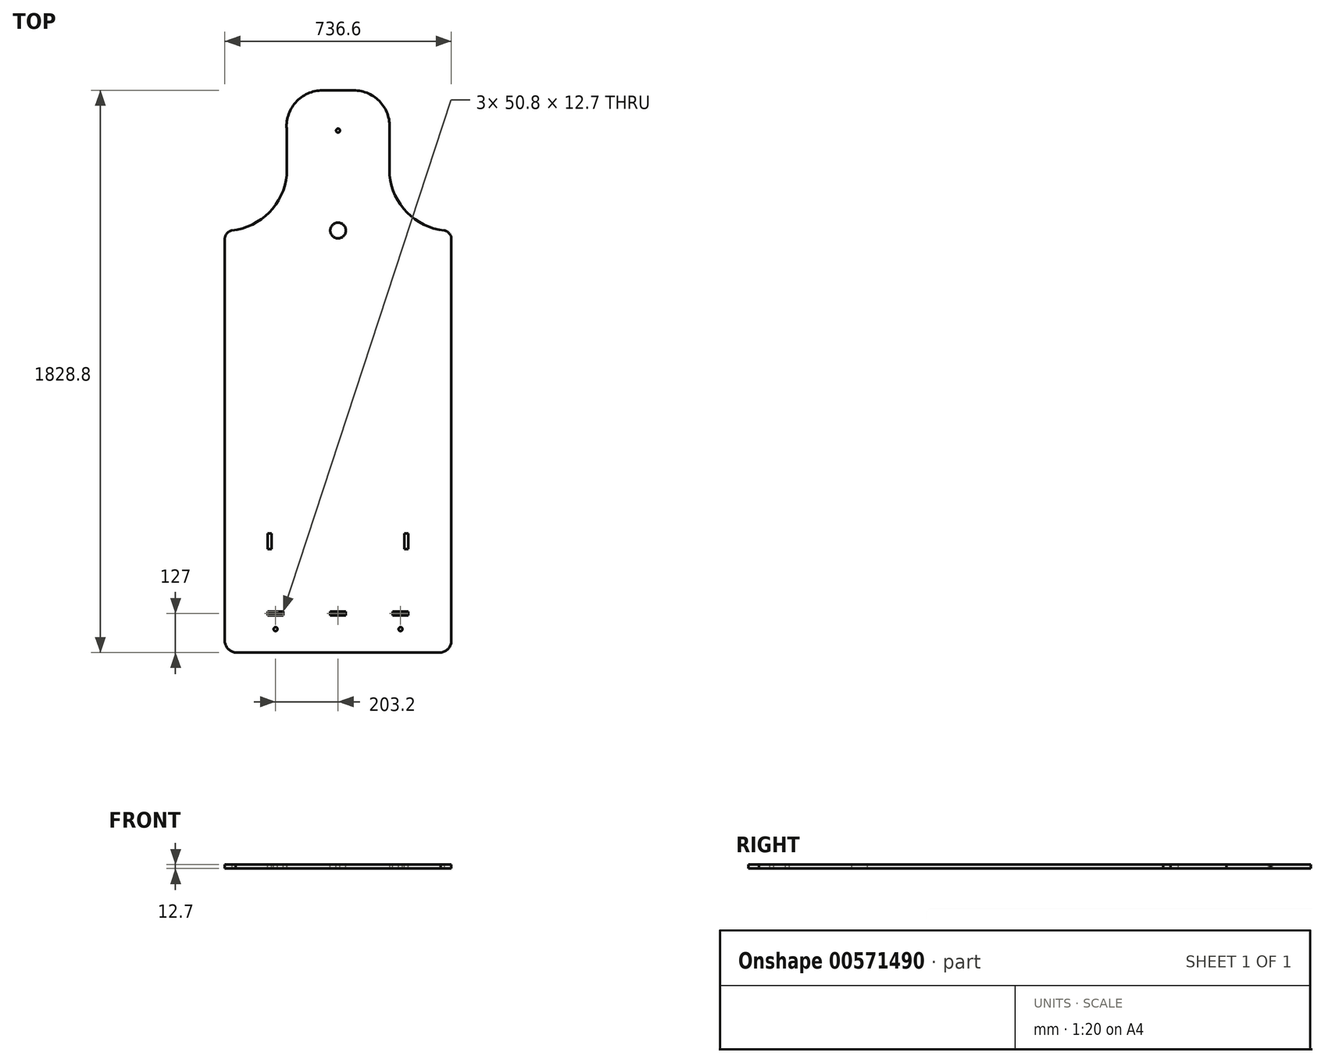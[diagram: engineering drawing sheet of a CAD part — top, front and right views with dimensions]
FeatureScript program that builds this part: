
annotation { "Feature Type Name" : "Feature", "Feature Type Description" : "" }
export const myFeature = defineFeature(function(context is Context, id is Id, definition is map)
    precondition{}
    {
        {
            var Q0;
            Q0=qCreatedBy(makeId("Top.planeOp"),FACE);
            var sketch = newSketch(context, id + "F0", { "sketchPlane" : qUnion([Q0])});
            skLineSegment(sketch, "E0.bottom", {"start": v(333.07, -685.8) * mm, "end": v(-333.07, -685.8) * mm});
            skLineSegment(sketch, "E0.left", {"start": v(368.3, -652.17) * mm, "end": v(368.3, 662.5) * mm});
            skLineSegment(sketch, "E0.right", {"start": v(-368.3, -652.17) * mm, "end": v(-368.3, 662.5) * mm});
            skPoint(sketch, "E0.middle", {"position": v(0, 0) * mm});
            skLineSegment(sketch, "E1", {"start": v(0, 685.8) * mm, "end": v(0, 1143) * mm, "construction": true});
            skPoint(sketch, "E1.endSnap0", {"position": v(0, 685.8) * mm});
            skLineSegment(sketch, "E2", {"start": v(0, 1143) * mm, "end": v(-50.8, 1143) * mm});
            skLineSegment(sketch, "E3", {"start": v(0, 1143) * mm, "end": v(50.8, 1143) * mm});
            skArc(sketch, "E4", {"start": v(-50.8, 1143) * mm, "mid": v(-138.23, 1103.66) * mm, "end": v(-166.78, 1012.14) * mm});
            skArc(sketch, "E5.MirrorCS", {"start": v(50.8, 1143) * mm, "mid": v(138.23, 1103.66) * mm, "end": v(166.78, 1012.14) * mm});
            skLineSegment(sketch, "E6", {"start": v(-166.78, 1012.14) * mm, "end": v(-166.78, 867.84) * mm});
            skArc(sketch, "E7", {"start": v(-345.55, 687.08) * mm, "mid": v(-224.28, 745.92) * mm, "end": v(-166.78, 867.84) * mm});
            skArc(sketch, "E8.MirrorCS", {"start": v(345.55, 687.08) * mm, "mid": v(224.28, 745.92) * mm, "end": v(166.78, 867.84) * mm});
            skLineSegment(sketch, "E9.MirrorCS", {"start": v(166.78, 1012.14) * mm, "end": v(166.78, 867.84) * mm});
            skArc(sketch, "E10", {"start": v(-345.55, 687.08) * mm, "mid": v(-360.85, 678.42) * mm, "end": v(-368.3, 662.5) * mm});
            skArc(sketch, "E11.MirrorCS", {"start": v(345.55, 687.08) * mm, "mid": v(360.85, 678.42) * mm, "end": v(368.3, 662.5) * mm});
            skPoint(sketch, "E12.orphan", {"position": v(-368.3, 685.8) * mm});
            skPoint(sketch, "E13.orphan", {"position": v(368.3, 685.8) * mm});
            skPoint(sketch, "E14.orphan", {"position": v(368.3, 655.07) * mm});
            skPoint(sketch, "E15.orphan", {"position": v(-368.3, 655.07) * mm});
            skArc(sketch, "E16", {"start": v(-368.3, -652.17) * mm, "mid": v(-356.47, -675.05) * mm, "end": v(-333.07, -685.8) * mm});
            skLineSegment(sketch, "E17", {"start": v(0, -685.8) * mm, "end": v(0, -615.78) * mm, "construction": true});
            skArc(sketch, "E18.MirrorCS", {"start": v(368.3, -652.17) * mm, "mid": v(356.47, -675.05) * mm, "end": v(333.07, -685.8) * mm});
            skPoint(sketch, "E19.orphan", {"position": v(-368.3, -685.8) * mm});
            skPoint(sketch, "E20.orphan", {"position": v(368.3, -685.8) * mm});
            skPoint(sketch, "E21.orphan", {"position": v(368.3, -640.65) * mm});
            skPoint(sketch, "E22.orphan", {"position": v(-368.3, -640.65) * mm});
            skSolve(sketch);
        }
        {
            var Q0;
            Q0 = qSketchRegion(id + "F0", true);
            extrude(context, id + "F1", {"entities" : qUnion([Q0]), "depth" : 12.7 * mm, "offsetDistance" : 25.4 * mm});
        }
        {
            var Q0;
            Q0=makeQuery(id+"F1.opExtrude","CAP_FACE",FACE,{"disambiguationData":[OSD([sQuery(id+"F0.wireOp",EDGE,"E0.bottom"),sQuery(id+"F0.wireOp",EDGE,"E0.left"),sQuery(id+"F0.wireOp",EDGE,"E0.right"),sQuery(id+"F0.wireOp",EDGE,"E2"),sQuery(id+"F0.wireOp",EDGE,"E3"),sQuery(id+"F0.wireOp",EDGE,"E4"),sQuery(id+"F0.wireOp",EDGE,"E5.MirrorCS"),sQuery(id+"F0.wireOp",EDGE,"E6"),sQuery(id+"F0.wireOp",EDGE,"E7"),sQuery(id+"F0.wireOp",EDGE,"E8.MirrorCS"),sQuery(id+"F0.wireOp",EDGE,"E9.MirrorCS"),sQuery(id+"F0.wireOp",EDGE,"E10"),sQuery(id+"F0.wireOp",EDGE,"E11.MirrorCS"),sQuery(id+"F0.wireOp",EDGE,"E16"),sQuery(id+"F0.wireOp",EDGE,"E18.MirrorCS")])],"isStart":false});
            var sketch = newSketch(context, id + "F2", { "sketchPlane" : qUnion([Q0])});
            skCircle(sketch, "E23", {"center": v(0, 1012.14) * mm, "radius": 6.35 * mm});
            skSolve(sketch);
        }
        {
            var Q0;
            Q0 = qSketchRegion(id + "F2", true);
            extrude(context, id + "F3", {"entities" : qUnion([Q0]), "operationType" : NewBodyOperationType.REMOVE, "oppositeDirection" : true, "depth" : 25.4 * mm, "offsetDistance" : 25.4 * mm});
        }
        {
            var Q0;
            Q0=makeQuery(id+"F1.opExtrude","CAP_FACE",FACE,{"disambiguationData":[OSD([sQuery(id+"F0.wireOp",EDGE,"E0.bottom"),sQuery(id+"F0.wireOp",EDGE,"E0.left"),sQuery(id+"F0.wireOp",EDGE,"E0.right"),sQuery(id+"F0.wireOp",EDGE,"E2"),sQuery(id+"F0.wireOp",EDGE,"E3"),sQuery(id+"F0.wireOp",EDGE,"E4"),sQuery(id+"F0.wireOp",EDGE,"E5.MirrorCS"),sQuery(id+"F0.wireOp",EDGE,"E6"),sQuery(id+"F0.wireOp",EDGE,"E7"),sQuery(id+"F0.wireOp",EDGE,"E8.MirrorCS"),sQuery(id+"F0.wireOp",EDGE,"E9.MirrorCS"),sQuery(id+"F0.wireOp",EDGE,"E10"),sQuery(id+"F0.wireOp",EDGE,"E11.MirrorCS"),sQuery(id+"F0.wireOp",EDGE,"E16"),sQuery(id+"F0.wireOp",EDGE,"E18.MirrorCS")])],"isStart":false});
            var sketch = newSketch(context, id + "F4", { "sketchPlane" : qUnion([Q0])});
            skPoint(sketch, "E24.endSnap0", {"position": v(0, -685.8) * mm});
            skPoint(sketch, "E25.endSnap0", {"position": v(0, -609.6) * mm});
            skCircle(sketch, "E26", {"center": v(-203.2, -609.6) * mm, "radius": 6.35 * mm});
            skCircle(sketch, "E27.MirrorC", {"center": v(203.2, -609.6) * mm, "radius": 6.35 * mm});
            skSolve(sketch);
        }
        {
            var Q0;
            Q0 = qSketchRegion(id + "F4", true);
            extrude(context, id + "F5", {"entities" : qUnion([Q0]), "operationType" : NewBodyOperationType.REMOVE, "oppositeDirection" : true, "depth" : 25.4 * mm, "offsetDistance" : 25.4 * mm});
        }
        {
            var Q0;
            Q0=makeQuery(id+"F1.opExtrude","CAP_FACE",FACE,{"disambiguationData":[OSD([sQuery(id+"F0.wireOp",EDGE,"E0.bottom"),sQuery(id+"F0.wireOp",EDGE,"E0.left"),sQuery(id+"F0.wireOp",EDGE,"E0.right"),sQuery(id+"F0.wireOp",EDGE,"E2"),sQuery(id+"F0.wireOp",EDGE,"E3"),sQuery(id+"F0.wireOp",EDGE,"E4"),sQuery(id+"F0.wireOp",EDGE,"E5.MirrorCS"),sQuery(id+"F0.wireOp",EDGE,"E6"),sQuery(id+"F0.wireOp",EDGE,"E7"),sQuery(id+"F0.wireOp",EDGE,"E8.MirrorCS"),sQuery(id+"F0.wireOp",EDGE,"E9.MirrorCS"),sQuery(id+"F0.wireOp",EDGE,"E10"),sQuery(id+"F0.wireOp",EDGE,"E11.MirrorCS"),sQuery(id+"F0.wireOp",EDGE,"E16"),sQuery(id+"F0.wireOp",EDGE,"E18.MirrorCS")])],"isStart":false});
            var sketch = newSketch(context, id + "F6", { "sketchPlane" : qUnion([Q0])});
            skLineSegment(sketch, "E28", {"start": v(-345.55, 687.08) * mm, "end": v(345.55, 687.08) * mm, "construction": true});
            skLineSegment(sketch, "E29", {"start": v(0, 687.08) * mm, "end": v(0, 77.48) * mm, "construction": true});
            skCircle(sketch, "E30", {"center": v(0, 687.08) * mm, "radius": 25.4 * mm});
            skSolve(sketch);
        }
        {
            var Q0;
            Q0 = qSketchRegion(id + "F6", true);
            extrude(context, id + "F7", {"entities" : qUnion([Q0]), "operationType" : NewBodyOperationType.REMOVE, "oppositeDirection" : true, "depth" : 25.4 * mm, "offsetDistance" : 25.4 * mm});
        }
        {
            var Q0;
            Q0=makeQuery(id+"F1.opExtrude","CAP_FACE",FACE,{"disambiguationData":[OSD([sQuery(id+"F0.wireOp",EDGE,"E0.bottom"),sQuery(id+"F0.wireOp",EDGE,"E0.left"),sQuery(id+"F0.wireOp",EDGE,"E0.right"),sQuery(id+"F0.wireOp",EDGE,"E2"),sQuery(id+"F0.wireOp",EDGE,"E3"),sQuery(id+"F0.wireOp",EDGE,"E4"),sQuery(id+"F0.wireOp",EDGE,"E5.MirrorCS"),sQuery(id+"F0.wireOp",EDGE,"E6"),sQuery(id+"F0.wireOp",EDGE,"E7"),sQuery(id+"F0.wireOp",EDGE,"E8.MirrorCS"),sQuery(id+"F0.wireOp",EDGE,"E9.MirrorCS"),sQuery(id+"F0.wireOp",EDGE,"E10"),sQuery(id+"F0.wireOp",EDGE,"E11.MirrorCS"),sQuery(id+"F0.wireOp",EDGE,"E16"),sQuery(id+"F0.wireOp",EDGE,"E18.MirrorCS")])],"isStart":false});
            var sketch = newSketch(context, id + "F8", { "sketchPlane" : qUnion([Q0])});
            skLineSegment(sketch, "E31.0", {"start": v(333.07, -558.8) * mm, "end": v(-333.07, -558.8) * mm, "construction": true});
            skLineSegment(sketch, "E32.bottom", {"start": v(25.4, -565.15) * mm, "end": v(-25.4, -565.15) * mm});
            skLineSegment(sketch, "E32.top", {"start": v(25.4, -552.45) * mm, "end": v(-25.4, -552.45) * mm});
            skLineSegment(sketch, "E32.left", {"start": v(25.4, -565.15) * mm, "end": v(25.4, -552.45) * mm});
            skLineSegment(sketch, "E32.right", {"start": v(-25.4, -565.15) * mm, "end": v(-25.4, -552.45) * mm});
            skPoint(sketch, "E32.middle", {"position": v(0, -558.8) * mm});
            skLineSegment(sketch, "E33.bottom", {"start": v(228.6, -685.8) * mm, "end": v(-228.6, -685.8) * mm, "construction": true});
            skLineSegment(sketch, "E34.0", {"start": v(333.07, -565.15) * mm, "end": v(-333.07, -565.15) * mm, "construction": true});
            skPoint(sketch, "E35.firstSnap0", {"position": v(-228.6, -558.8) * mm});
            skLineSegment(sketch, "E35.bottom", {"start": v(-228.6, -552.45) * mm, "end": v(-228.6, -552.45) * mm});
            skLineSegment(sketch, "E35.top", {"start": v(-228.6, -558.8) * mm, "end": v(-228.6, -558.8) * mm});
            skLineSegment(sketch, "E35.left", {"start": v(-228.6, -552.45) * mm, "end": v(-228.6, -558.8) * mm, "construction": true});
            skLineSegment(sketch, "E35.right", {"start": v(-228.6, -552.45) * mm, "end": v(-228.6, -558.8) * mm, "construction": true});
            skLineSegment(sketch, "E36.bottom", {"start": v(-228.6, -552.45) * mm, "end": v(-177.8, -552.45) * mm});
            skLineSegment(sketch, "E36.top", {"start": v(-228.6, -565.15) * mm, "end": v(-177.8, -565.15) * mm});
            skLineSegment(sketch, "E36.left", {"start": v(-228.6, -552.45) * mm, "end": v(-228.6, -565.15) * mm});
            skLineSegment(sketch, "E36.right", {"start": v(-177.8, -552.45) * mm, "end": v(-177.8, -565.15) * mm});
            skLineSegment(sketch, "E37", {"start": v(0, -558.8) * mm, "end": v(0, -513.4) * mm, "construction": true});
            skLineSegment(sketch, "E38.MirrorCS", {"start": v(228.6, -552.45) * mm, "end": v(177.8, -552.45) * mm});
            skLineSegment(sketch, "E39.MirrorCS", {"start": v(177.8, -552.45) * mm, "end": v(177.8, -565.15) * mm});
            skLineSegment(sketch, "E40", {"start": v(177.8, -565.15) * mm, "end": v(228.6, -565.15) * mm});
            skLineSegment(sketch, "E41", {"start": v(228.6, -565.15) * mm, "end": v(228.6, -552.45) * mm});
            skLineSegment(sketch, "E42", {"start": v(228.6, -552.45) * mm, "end": v(228.6, -349.25) * mm, "construction": true});
            skLineSegment(sketch, "E43", {"start": v(-228.6, -552.45) * mm, "end": v(-228.6, -349.25) * mm, "construction": true});
            skLineSegment(sketch, "E44.bottom", {"start": v(-228.6, -349.25) * mm, "end": v(-215.9, -349.25) * mm});
            skLineSegment(sketch, "E44.top", {"start": v(-228.6, -298.45) * mm, "end": v(-215.9, -298.45) * mm});
            skLineSegment(sketch, "E44.left", {"start": v(-228.6, -349.25) * mm, "end": v(-228.6, -298.45) * mm});
            skLineSegment(sketch, "E44.right", {"start": v(-215.9, -349.25) * mm, "end": v(-215.9, -298.45) * mm});
            skLineSegment(sketch, "E45.bottom", {"start": v(228.6, -349.25) * mm, "end": v(215.9, -349.25) * mm});
            skLineSegment(sketch, "E45.top", {"start": v(228.6, -298.45) * mm, "end": v(215.9, -298.45) * mm});
            skLineSegment(sketch, "E45.left", {"start": v(228.6, -349.25) * mm, "end": v(228.6, -298.45) * mm});
            skLineSegment(sketch, "E45.right", {"start": v(215.9, -349.25) * mm, "end": v(215.9, -298.45) * mm});
            skSolve(sketch);
        }
        {
            var Q0;
            Q0 = qSketchRegion(id + "F8", true);
            extrude(context, id + "F9", {"entities" : qUnion([Q0]), "operationType" : NewBodyOperationType.REMOVE, "oppositeDirection" : true, "depth" : 25.4 * mm, "offsetDistance" : 25.4 * mm});
        }
    });
